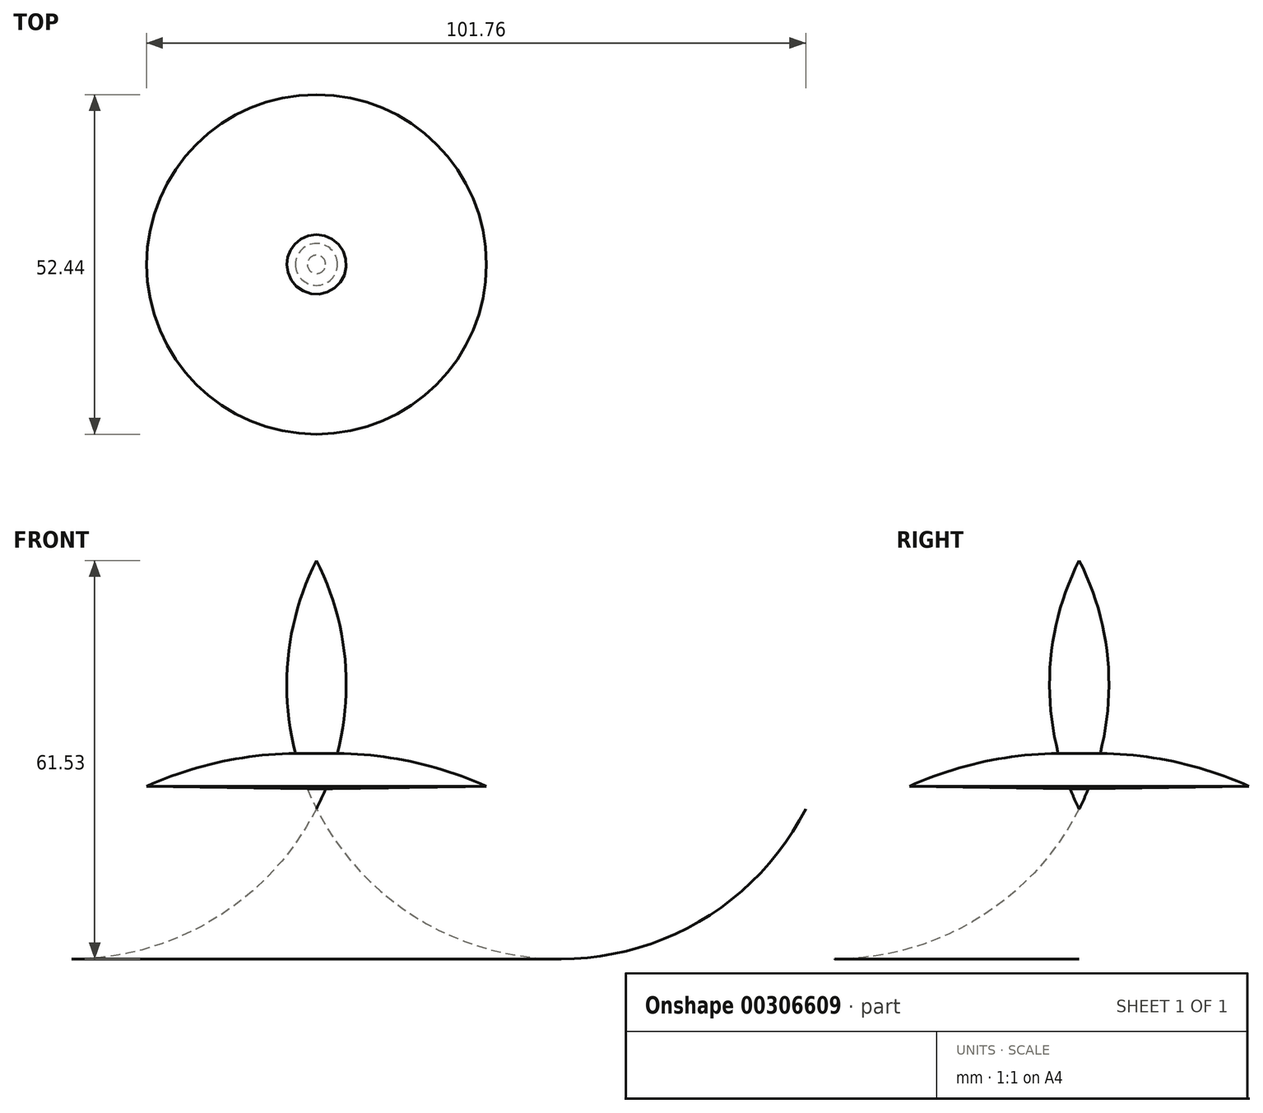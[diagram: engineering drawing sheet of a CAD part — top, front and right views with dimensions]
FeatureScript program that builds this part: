
annotation { "Feature Type Name" : "Feature", "Feature Type Description" : "" }
export const myFeature = defineFeature(function(context is Context, id is Id, definition is map)
    precondition{}
    {
        {
            var Q0;
            Q0=qCreatedBy(makeId("Front.planeOp"),FACE);
            var sketch = newSketch(context, id + "F0", { "sketchPlane" : qUnion([Q0])});
            skArc(sketch, "E0", {"start": v(-1.97, -3.41) * mm, "mid": v(2.62, 15.76) * mm, "end": v(-1.97, 34.94) * mm});
            skLineSegment(sketch, "E1", {"start": v(-0.56, -0.33) * mm, "end": v(24.25, 0.07) * mm});
            skArc(sketch, "E2", {"start": v(24.25, 0.07) * mm, "mid": v(13.02, 3.8) * mm, "end": v(1.27, 5.16) * mm});
            skLineSegment(sketch, "E3", {"start": v(-1.97, 34.94) * mm, "end": v(-1.97, -3.41) * mm});
            skSolve(sketch);
        }
        {
            var Q0;
            Q0 = qSketchRegion(id + "F0", true);
            var Q1;
            Q1=sQuery(id+"F0.wireOp",EDGE,"E3");
            revolve(context, id + "F1", {"entities" : qUnion([Q0]), "axis" : qUnion([Q1]), "revolveType" : RevolveType.FULL});
        }
    });
